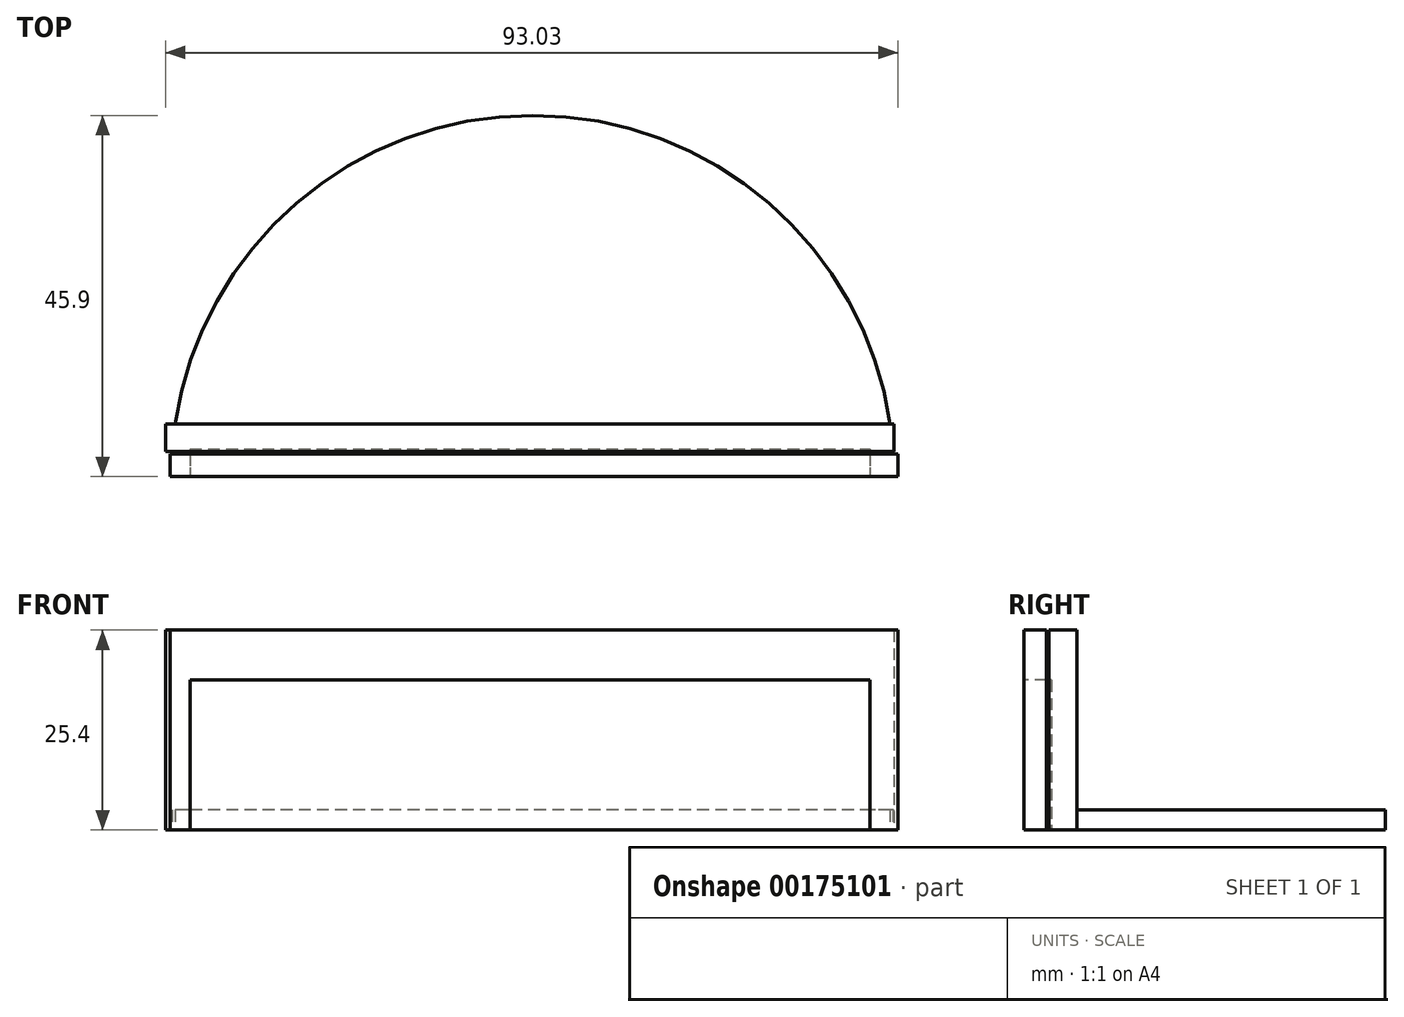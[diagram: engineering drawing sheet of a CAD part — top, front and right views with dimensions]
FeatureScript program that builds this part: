
annotation { "Feature Type Name" : "Feature", "Feature Type Description" : "" }
export const myFeature = defineFeature(function(context is Context, id is Id, definition is map)
    precondition{}
    {
        {
            var Q0;
            Q0=qCreatedBy(makeId("Top.planeOp"),FACE);
            var sketch = newSketch(context, id + "F0", { "sketchPlane" : qUnion([Q0])});
            skArc(sketch, "E0", {"start": v(45.9, 0) * mm, "mid": v(0, 45.9) * mm, "end": v(-45.9, 0) * mm});
            skLineSegment(sketch, "E1", {"start": v(-45.9, 0) * mm, "end": v(45.9, 0) * mm});
            skSolve(sketch);
        }
        {
            var Q0;
            Q0 = qSketchRegion(id + "F0", true);
            extrude(context, id + "F1", {"entities" : qUnion([Q0]), "depth" : 2.54 * mm});
        }
        {
            var Q0;
            Q0=qCreatedBy(makeId("Top.planeOp"),FACE);
            var sketch = newSketch(context, id + "F2", { "sketchPlane" : qUnion([Q0])});
            skLineSegment(sketch, "E2.bottom", {"start": v(-46.09, 0) * mm, "end": v(46.4, 0) * mm});
            skLineSegment(sketch, "E2.top", {"start": v(-46.09, 2.88) * mm, "end": v(46.4, 2.88) * mm});
            skLineSegment(sketch, "E2.left", {"start": v(-46.09, 0) * mm, "end": v(-46.09, 2.88) * mm});
            skLineSegment(sketch, "E2.right", {"start": v(46.4, 0) * mm, "end": v(46.4, 2.88) * mm});
            skSolve(sketch);
        }
        {
            var Q0;
            Q0 = qSketchRegion(id + "F2", true);
            extrude(context, id + "F3", {"entities" : qUnion([Q0]), "operationType" : NewBodyOperationType.ADD, "depth" : 25.4 * mm});
        }
        {
            var Q0;
            Q0=qCreatedBy(makeId("Top.planeOp"),FACE);
            var sketch = newSketch(context, id + "F4", { "sketchPlane" : qUnion([Q0])});
            skLineSegment(sketch, "E3.bottom", {"start": v(-46.62, 3.2) * mm, "end": v(45.87, 3.2) * mm});
            skLineSegment(sketch, "E3.top", {"start": v(-46.62, 6.72) * mm, "end": v(45.87, 6.72) * mm});
            skLineSegment(sketch, "E3.left", {"start": v(-46.62, 3.2) * mm, "end": v(-46.62, 6.72) * mm});
            skLineSegment(sketch, "E3.right", {"start": v(45.87, 3.2) * mm, "end": v(45.87, 6.72) * mm});
            skSolve(sketch);
        }
        {
            var Q0;
            Q0 = qSketchRegion(id + "F4", true);
            extrude(context, id + "F5", {"entities" : qUnion([Q0]), "operationType" : NewBodyOperationType.ADD, "depth" : 25.4 * mm});
        }
        {
            var Q0;
            Q0=qCreatedBy(makeId("Top.planeOp"),FACE);
            var sketch = newSketch(context, id + "F6", { "sketchPlane" : qUnion([Q0])});
            skLineSegment(sketch, "E4.bottom", {"start": v(-43.54, 3.5) * mm, "end": v(42.82, 3.5) * mm});
            skLineSegment(sketch, "E4.top", {"start": v(-43.54, 0) * mm, "end": v(42.82, 0) * mm});
            skLineSegment(sketch, "E4.left", {"start": v(-43.54, 3.5) * mm, "end": v(-43.54, 0) * mm});
            skLineSegment(sketch, "E4.right", {"start": v(42.82, 3.5) * mm, "end": v(42.82, 0) * mm});
            skSolve(sketch);
        }
        {
            var Q0;
            Q0 = qSketchRegion(id + "F6", true);
            extrude(context, id + "F7", {"entities" : qUnion([Q0]), "operationType" : NewBodyOperationType.REMOVE, "depth" : 19.05 * mm});
        }
    });
